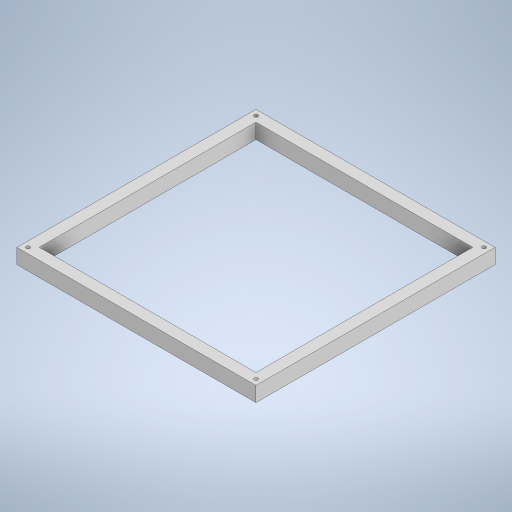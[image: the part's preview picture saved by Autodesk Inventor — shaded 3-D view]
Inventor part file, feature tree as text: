
AUTODESK INVENTOR PART (.ipt)
format: ipt  version: 2023 (Build 270158000, 158)  size: 278,528 bytes
history: native  units: in
note: dims shown in document units (in); Inventor stores cm internally (conversion verified against a paired STEP export)
features: sketch x3, extrude x2, projected_geometry x2
ambient origin geometry x8: Origin, YZ Plane, XZ Plane, XY Plane, X Axis, Y Axis, Z Axis, Center Point
bodies: Solid1 (feature_tree)
feature tree (7):
  extrude  "Extrusion1"  Depth=4.0in
  extrude  "Extrusion2"  Depth=0.25in TaperAngle=0.0deg
  sketch  "Sketch3"  dims[d13=0.5in d14=1.5625in d15=1.1562in d16=0.5in d17=0.9063in d18=0.25in d20=0.0625in d21=0.0938in d22=0.0938in d23=0.7874in d25=3.8125in d26=0.7874in d28=3.8125in d31=0.25in d32=0.0in]
  sketch  "Sketch1"  dims[d0=4.0in d1=4.0in]
  sketch  "Sketch2"  dims[d2=0.1875in d11=0.25in d12=0.0in]
  projected_geometry  "Projected Loop1"
  projected_geometry  "Projected Loop2"
